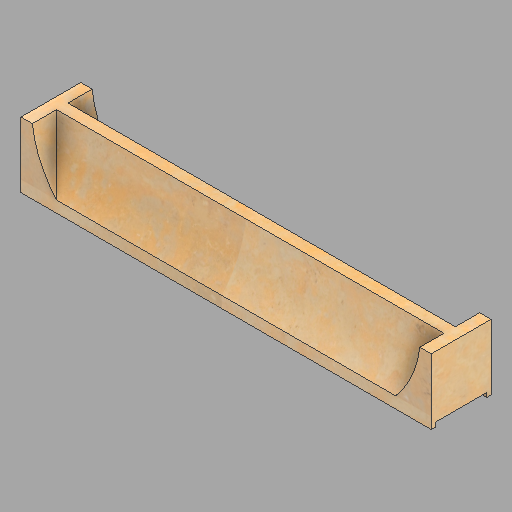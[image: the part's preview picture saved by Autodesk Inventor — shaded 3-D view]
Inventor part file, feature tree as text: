
AUTODESK INVENTOR PART (.ipt)
format: ipt  version: 2022.2 (Build 262287010, 287A)  size: 252,928 bytes
history: native  units: in
note: dims shown in document units (in); Inventor stores cm internally (conversion verified against a paired STEP export)
features: direct_edit x1, other x1, revolve x1
ambient origin geometry x8: Origin, YZ Plane, XZ Plane, XY Plane, X Axis, Y Axis, Z Axis, Center Point
bodies: Solid1 (feature_tree)
feature tree (3):
  direct_edit  "Direct Edit1"
  other  "West (6)"
  revolve  "Rotate1"  Angle=90.0deg
